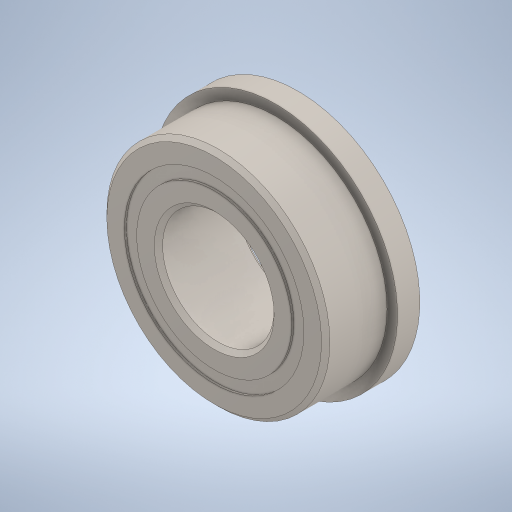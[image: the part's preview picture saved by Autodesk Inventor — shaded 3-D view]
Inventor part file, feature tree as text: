
AUTODESK INVENTOR PART (.ipt)
format: ipt  version: 2024 (Build 280153000, 153)  size: 767,488 bytes
history: native  units: in
note: dims shown in document units (in); Inventor stores cm internally (conversion verified against a paired STEP export)
features: other x11, revolve x5
ambient origin geometry x8: Origin, YZ Plane, XZ Plane, XY Plane, X Axis, Y Axis, Z Axis, Center Point
bodies: Solid1 (feature_tree), Solid2 (feature_tree), Solid3 (feature_tree), Solid4 (feature_tree), Solid5 (feature_tree), Solid6 (feature_tree), Solid7 (feature_tree), Solid8 (feature_tree), Solid9 (feature_tree), Solid10 (feature_tree), Solid11 (feature_tree), Solid12 (feature_tree), Solid13 (feature_tree), Solid14 (feature_tree), Solid15 (feature_tree), Solid16 (feature_tree)
feature tree (16):
  revolve  "Revolve3"  [1 undecoded]
  revolve  "Revolve4"  [1 undecoded]
  other  "CirPattern1[1]"
  other  "CirPattern1[2]"
  other  "CirPattern1[3]"
  other  "CirPattern1[4]"
  other  "CirPattern1[5]"
  other  "CirPattern1[6]"
  other  "CirPattern1[7]"
  other  "CirPattern1[8]"
  other  "CirPattern1[9]"
  other  "CirPattern1[10]"
  other  "CirPattern1[11]"
  revolve  "Revolve5[1]"  [1 undecoded]
  revolve  "Revolve5[2]"  [1 undecoded]
  revolve  "Revolve6"  [1 undecoded]
note: 5 required parameter values undecoded (feature->parameter linkage not recoverable at this tier; creation-order binding heuristic only, values carry confidence <= 0.55)
